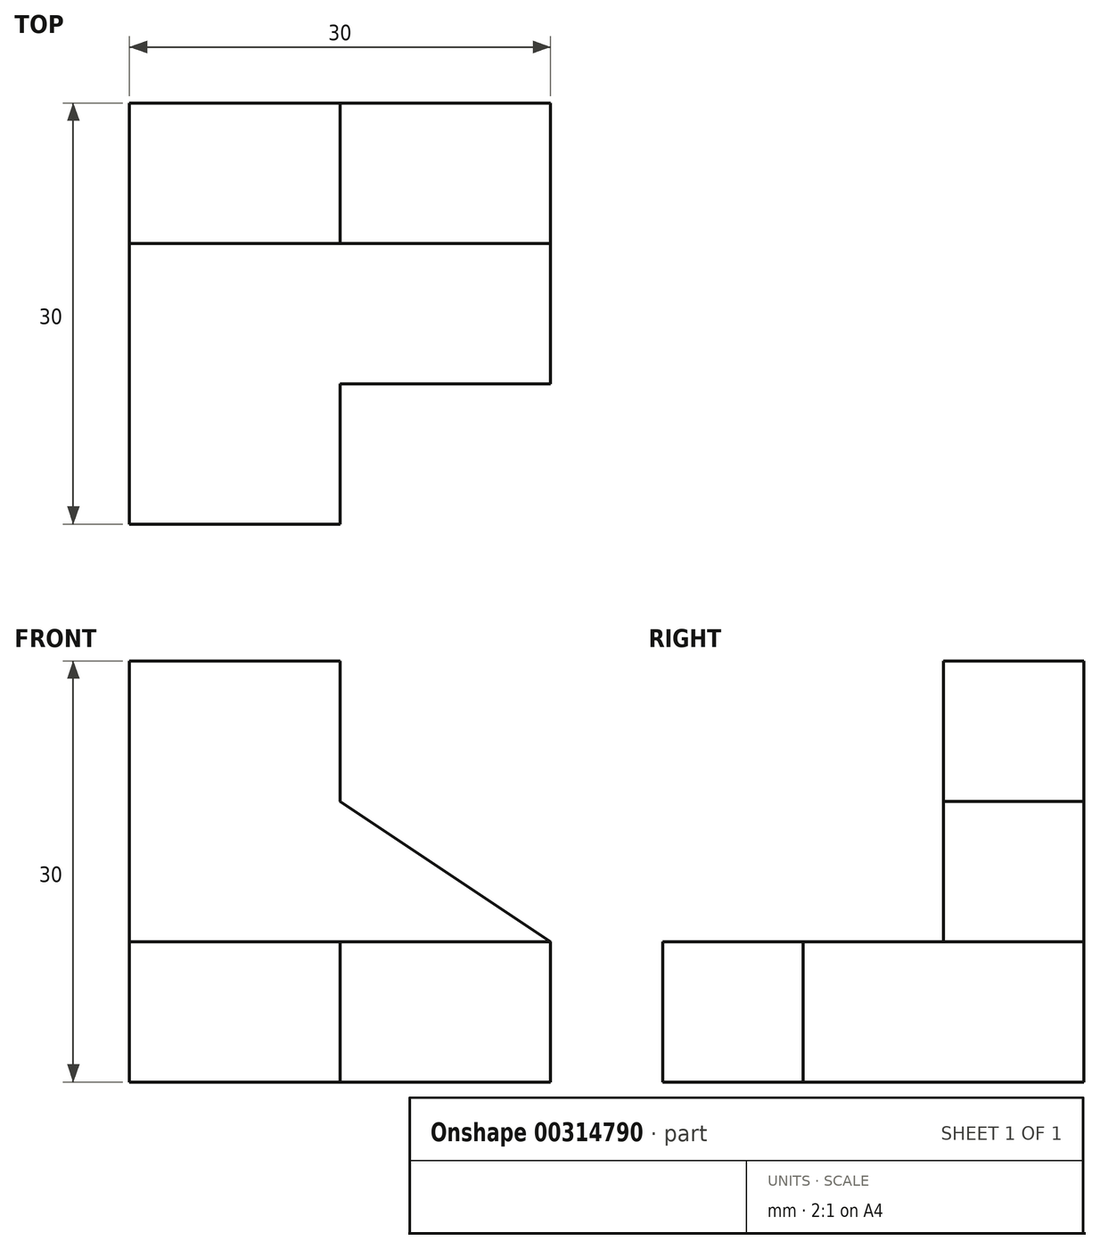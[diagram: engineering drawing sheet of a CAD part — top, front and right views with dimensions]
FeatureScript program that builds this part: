
annotation { "Feature Type Name" : "Feature", "Feature Type Description" : "" }
export const myFeature = defineFeature(function(context is Context, id is Id, definition is map)
    precondition{}
    {
        {
            var Q0;
            Q0=qCreatedBy(makeId("Right.planeOp"),FACE);
            var sketch = newSketch(context, id + "F0", { "sketchPlane" : qUnion([Q0])});
            skLineSegment(sketch, "E0.bottom", {"start": v(0, 0) * mm, "end": v(30, 0) * mm});
            skLineSegment(sketch, "E0.top", {"start": v(0, 30) * mm, "end": v(30, 30) * mm});
            skLineSegment(sketch, "E0.left", {"start": v(0, 0) * mm, "end": v(0, 30) * mm});
            skLineSegment(sketch, "E0.right", {"start": v(30, 0) * mm, "end": v(30, 30) * mm});
            skLineSegment(sketch, "E1.bottom", {"start": v(0, 30) * mm, "end": v(20, 30) * mm});
            skLineSegment(sketch, "E1.top", {"start": v(0, 10) * mm, "end": v(20, 10) * mm});
            skLineSegment(sketch, "E1.left", {"start": v(0, 30) * mm, "end": v(0, 10) * mm});
            skLineSegment(sketch, "E1.right", {"start": v(20, 30) * mm, "end": v(20, 10) * mm});
            skSolve(sketch);
        }
        {
            var Q0;
            {var subQ1=sQuery(id+"F0.wireOp",EDGE,"E0.bottom");Q0=makeQuery(id+"F0.imprint","IMPRINT",FACE,{"disambiguationData":[TD([[makeQuery(id+"F0.imprint","IMPRINT",EDGE,{"derivedFrom":subQ1}),1.0]])]});}
            extrude(context, id + "F1", {"entities" : qUnion([Q0]), "depth" : 30 * mm, "symmetric" : true});
        }
        {
            var Q0;
            Q0=makeQuery(id+"F1.opExtrude","SWEPT_FACE",FACE,{"disambiguationData":[OSD([sQuery(id+"F0.wireOp",EDGE,"E1.right")])]});
            var sketch = newSketch(context, id + "F2", { "sketchPlane" : qUnion([Q0])});
            skLineSegment(sketch, "E2", {"start": v(0, 30) * mm, "end": v(0, 20) * mm});
            skPoint(sketch, "E2.endSnap0", {"position": v(15, 20) * mm});
            skLineSegment(sketch, "E3", {"start": v(0, 20) * mm, "end": v(15, 10) * mm});
            skSolve(sketch);
        }
        {
            var Q0;
            Q0 = qSketchRegion(id + "F2", true);
            var Q1;
            {var subQ0=sQuery(id+"F2.wireOp",EDGE,"E2");Q1=makeQuery(id+"F2.imprint","IMPRINT",FACE,{"disambiguationData":[TD([[makeQuery(id+"F2.imprint","IMPRINT",EDGE,{"derivedFrom":subQ0}),1.0]])]});}
            extrude(context, id + "F3", {"entities" : qUnion([Q0, Q1]), "operationType" : NewBodyOperationType.REMOVE, "endBound" : BoundingType.THROUGH_ALL, "oppositeDirection" : true, "depth" : 25 * mm});
        }
        {
            var Q0;
            Q0=makeQuery(id+"F1.opExtrude","SWEPT_FACE",FACE,{"disambiguationData":[OSD([sQuery(id+"F0.wireOp",EDGE,"E1.top")])]});
            var sketch = newSketch(context, id + "F4", { "sketchPlane" : qUnion([Q0])});
            skLineSegment(sketch, "E4", {"start": v(0, 0) * mm, "end": v(0, 10) * mm});
            skPoint(sketch, "E4.endSnap0", {"position": v(15, 10) * mm});
            skLineSegment(sketch, "E5", {"start": v(0, 10) * mm, "end": v(15, 10) * mm});
            skSolve(sketch);
        }
        {
            var Q0;
            Q0 = qSketchRegion(id + "F4", true);
            var Q1;
            {var subQ0=sQuery(id+"F4.wireOp",EDGE,"E4");Q1=makeQuery(id+"F4.imprint","IMPRINT",FACE,{"disambiguationData":[TD([[makeQuery(id+"F4.imprint","IMPRINT",EDGE,{"derivedFrom":subQ0}),-1.0]])]});}
            extrude(context, id + "F5", {"entities" : qUnion([Q0, Q1]), "operationType" : NewBodyOperationType.REMOVE, "endBound" : BoundingType.THROUGH_ALL, "oppositeDirection" : true, "depth" : 25 * mm});
        }
    });
